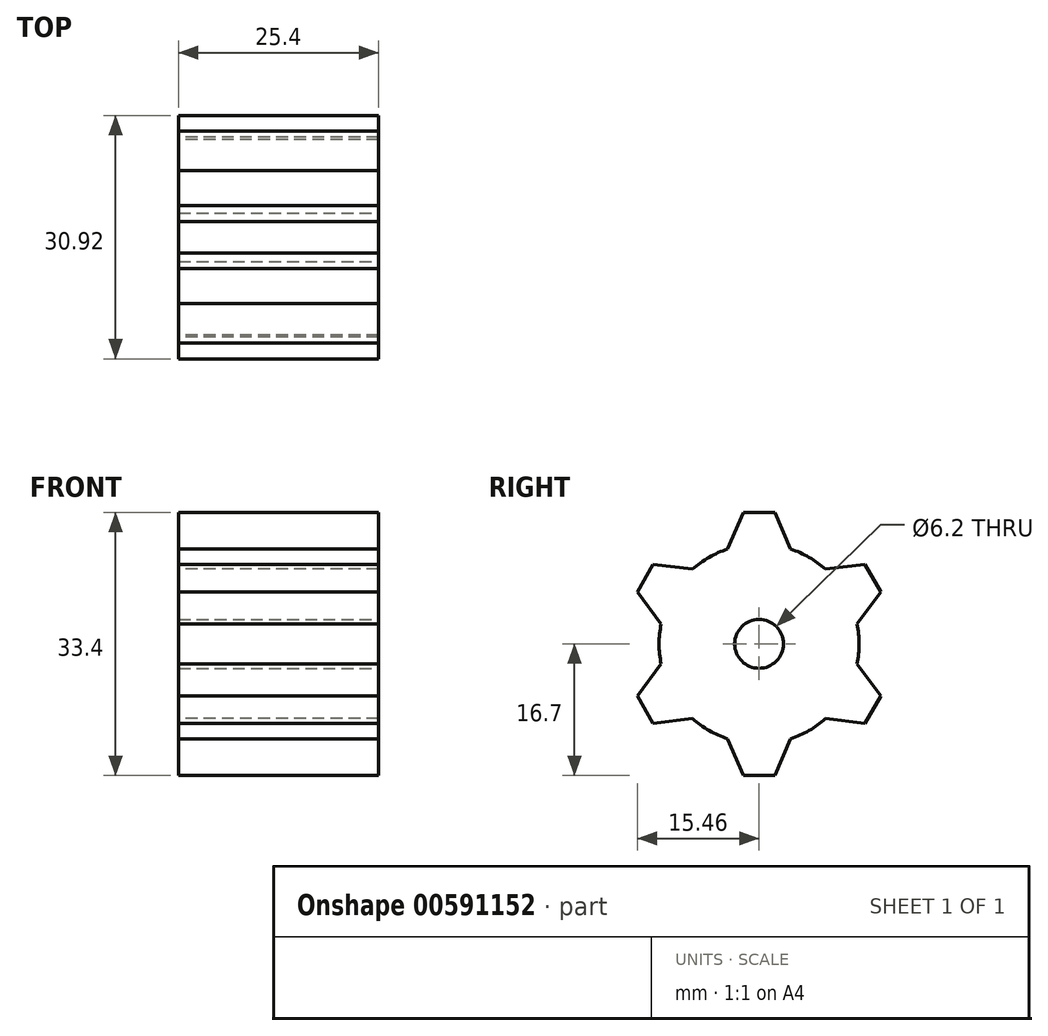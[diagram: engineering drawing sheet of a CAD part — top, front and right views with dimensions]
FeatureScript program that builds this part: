
annotation { "Feature Type Name" : "Feature", "Feature Type Description" : "" }
export const myFeature = defineFeature(function(context is Context, id is Id, definition is map)
    precondition{}
    {
        {
            var Q0;
            Q0=qCreatedBy(makeId("Right.planeOp"),FACE);
            var sketch = newSketch(context, id + "F0", { "sketchPlane" : qUnion([Q0])});
            skCircle(sketch, "E0", {"center": v(0, 0) * mm, "radius": 12.7 * mm});
            skLineSegment(sketch, "E1", {"start": v(0, 0) * mm, "end": v(0, 12.7) * mm, "construction": true});
            skLineSegment(sketch, "E2", {"start": v(0, 16.7) * mm, "end": v(-2, 16.7) * mm});
            skLineSegment(sketch, "E3", {"start": v(-2, 16.7) * mm, "end": v(-4, 12.05) * mm});
            skLineSegment(sketch, "E4.MirrorCS", {"start": v(0, 16.7) * mm, "end": v(2, 16.7) * mm});
            skLineSegment(sketch, "E5.MirrorCS", {"start": v(2, 16.7) * mm, "end": v(4, 12.05) * mm});
            skLineSegment(sketch, "E6.1.0", {"start": v(-15.46, 6.62) * mm, "end": v(-12.44, 2.56) * mm});
            skLineSegment(sketch, "E6.1.1", {"start": v(-14.46, 8.35) * mm, "end": v(-15.46, 6.62) * mm});
            skLineSegment(sketch, "E6.1.2", {"start": v(-14.46, 8.35) * mm, "end": v(-13.46, 10.08) * mm});
            skLineSegment(sketch, "E6.1.3", {"start": v(-13.46, 10.08) * mm, "end": v(-8.44, 9.5) * mm});
            skLineSegment(sketch, "E6.2.0", {"start": v(-13.46, -10.08) * mm, "end": v(-8.44, -9.5) * mm});
            skLineSegment(sketch, "E6.2.1", {"start": v(-14.46, -8.35) * mm, "end": v(-13.46, -10.08) * mm});
            skLineSegment(sketch, "E6.2.2", {"start": v(-14.46, -8.35) * mm, "end": v(-15.46, -6.62) * mm});
            skLineSegment(sketch, "E6.2.3", {"start": v(-15.46, -6.62) * mm, "end": v(-12.44, -2.56) * mm});
            skLineSegment(sketch, "E6.3.0", {"start": v(2, -16.7) * mm, "end": v(4, -12.05) * mm});
            skLineSegment(sketch, "E6.3.1", {"start": v(0, -16.7) * mm, "end": v(2, -16.7) * mm});
            skLineSegment(sketch, "E6.3.2", {"start": v(0, -16.7) * mm, "end": v(-2, -16.7) * mm});
            skLineSegment(sketch, "E6.3.3", {"start": v(-2, -16.7) * mm, "end": v(-4, -12.05) * mm});
            skLineSegment(sketch, "E6.4.0", {"start": v(15.46, -6.62) * mm, "end": v(12.44, -2.56) * mm});
            skLineSegment(sketch, "E6.4.1", {"start": v(14.46, -8.35) * mm, "end": v(15.46, -6.62) * mm});
            skLineSegment(sketch, "E6.4.2", {"start": v(14.46, -8.35) * mm, "end": v(13.46, -10.08) * mm});
            skLineSegment(sketch, "E6.4.3", {"start": v(13.46, -10.08) * mm, "end": v(8.44, -9.5) * mm});
            skLineSegment(sketch, "E6.5.0", {"start": v(13.46, 10.08) * mm, "end": v(8.44, 9.5) * mm});
            skLineSegment(sketch, "E6.5.1", {"start": v(14.46, 8.35) * mm, "end": v(13.46, 10.08) * mm});
            skLineSegment(sketch, "E6.5.2", {"start": v(14.46, 8.35) * mm, "end": v(15.46, 6.62) * mm});
            skLineSegment(sketch, "E6.5.3", {"start": v(15.46, 6.62) * mm, "end": v(12.44, 2.56) * mm});
            skSolve(sketch);
        }
        {
            var Q0;
            Q0=qSketchRegion(id+"F0",true);
            extrude(context, id + "F1", {"entities" : qUnion([Q0]), "depth" : 25.4 * mm, "offsetDistance" : 25.4 * mm});
        }
        {
            var Q0;
            Q0=makeQuery(id+"F1.opExtrude","CAP_FACE",FACE,{"disambiguationData":[OSD([sQuery(id+"F0.wireOp",EDGE,"E0"),sQuery(id+"F0.wireOp",EDGE,"E2"),sQuery(id+"F0.wireOp",EDGE,"E3"),sQuery(id+"F0.wireOp",EDGE,"E4.MirrorCS"),sQuery(id+"F0.wireOp",EDGE,"E5.MirrorCS"),sQuery(id+"F0.wireOp",EDGE,"E6.1.0"),sQuery(id+"F0.wireOp",EDGE,"E6.1.1"),sQuery(id+"F0.wireOp",EDGE,"E6.1.2"),sQuery(id+"F0.wireOp",EDGE,"E6.1.3"),sQuery(id+"F0.wireOp",EDGE,"E6.2.0"),sQuery(id+"F0.wireOp",EDGE,"E6.2.1"),sQuery(id+"F0.wireOp",EDGE,"E6.2.2"),sQuery(id+"F0.wireOp",EDGE,"E6.2.3"),sQuery(id+"F0.wireOp",EDGE,"E6.3.0"),sQuery(id+"F0.wireOp",EDGE,"E6.3.1"),sQuery(id+"F0.wireOp",EDGE,"E6.3.2"),sQuery(id+"F0.wireOp",EDGE,"E6.3.3"),sQuery(id+"F0.wireOp",EDGE,"E6.4.0"),sQuery(id+"F0.wireOp",EDGE,"E6.4.1"),sQuery(id+"F0.wireOp",EDGE,"E6.4.2"),sQuery(id+"F0.wireOp",EDGE,"E6.4.3"),sQuery(id+"F0.wireOp",EDGE,"E6.5.0"),sQuery(id+"F0.wireOp",EDGE,"E6.5.1"),sQuery(id+"F0.wireOp",EDGE,"E6.5.2"),sQuery(id+"F0.wireOp",EDGE,"E6.5.3")])],"isStart":false});
            var sketch = newSketch(context, id + "F2", { "sketchPlane" : qUnion([Q0])});
            skArc(sketch, "E7", {"start": v(-2.08, 2.3) * mm, "mid": v(0, -3.1) * mm, "end": v(2.08, 2.3) * mm});
            skArc(sketch, "E8", {"start": v(-2.08, 2.3) * mm, "mid": v(0, 3.1) * mm, "end": v(2.08, 2.3) * mm});
            skSolve(sketch);
        }
        {
            var Q0;
            Q0=makeQuery(id+"F2.imprint","IMPRINT",FACE,{"disambiguationData":[TD([[makeQuery(id+"F2.imprint","IMPRINT",EDGE,{"derivedFrom":sQuery(id+"F2.wireOp",EDGE,"E7")}),1.0]])]});
            extrude(context, id + "F3", {"entities" : qUnion([Q0]), "operationType" : NewBodyOperationType.REMOVE, "oppositeDirection" : true, "depth" : 25.4 * mm, "offsetDistance" : 25.4 * mm});
        }
    });
